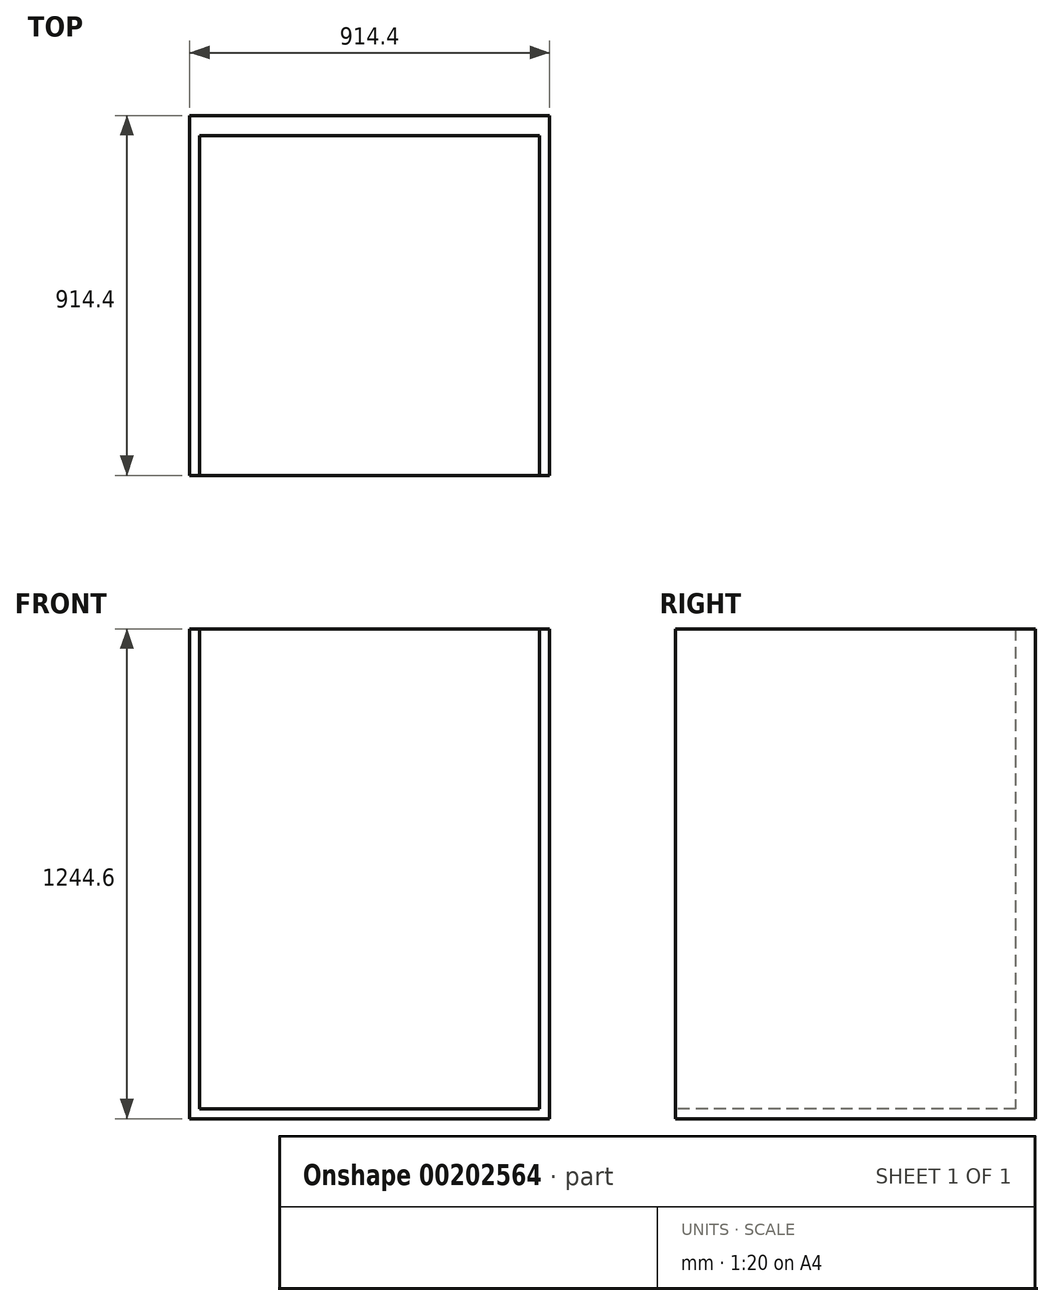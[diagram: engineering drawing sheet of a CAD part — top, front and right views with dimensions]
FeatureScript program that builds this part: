
annotation { "Feature Type Name" : "Feature", "Feature Type Description" : "" }
export const myFeature = defineFeature(function(context is Context, id is Id, definition is map)
    precondition{}
    {
        {
            var Q0;
            Q0=qCreatedBy(makeId("Top.planeOp"),FACE);
            var sketch = newSketch(context, id + "F0", { "sketchPlane" : qUnion([Q0])});
            skLineSegment(sketch, "E0.bottom", {"start": v(0, 0) * mm, "end": v(914.4, 0) * mm});
            skLineSegment(sketch, "E0.top", {"start": v(0, 914.4) * mm, "end": v(914.4, 914.4) * mm});
            skLineSegment(sketch, "E0.left", {"start": v(0, 0) * mm, "end": v(0, 914.4) * mm});
            skLineSegment(sketch, "E0.right", {"start": v(914.4, 0) * mm, "end": v(914.4, 914.4) * mm});
            skSolve(sketch);
        }
        {
            var Q0;
            Q0=makeQuery(id+"F0.imprint","IMPRINT",FACE,{"disambiguationData":[TD([[makeQuery(id+"F0.imprint","IMPRINT",EDGE,{"derivedFrom":sQuery(id+"F0.wireOp",EDGE,"E0.bottom")}),1.0]])]});
            extrude(context, id + "F1", {"entities" : qUnion([Q0]), "depth" : 25.4 * mm});
        }
        {
            var Q0;
            Q0=makeQuery(id+"F1.opExtrude","CAP_FACE",FACE,{"disambiguationData":[OSD([sQuery(id+"F0.wireOp",EDGE,"E0.bottom"),sQuery(id+"F0.wireOp",EDGE,"E0.top"),sQuery(id+"F0.wireOp",EDGE,"E0.left"),sQuery(id+"F0.wireOp",EDGE,"E0.right")])],"isStart":false});
            var sketch = newSketch(context, id + "F2", { "sketchPlane" : qUnion([Q0])});
            skLineSegment(sketch, "E1", {"start": v(0, 0) * mm, "end": v(25.4, 0) * mm});
            skLineSegment(sketch, "E2", {"start": v(25.4, 0) * mm, "end": v(25.4, 863.6) * mm});
            skLineSegment(sketch, "E3", {"start": v(25.4, 863.6) * mm, "end": v(889, 863.6) * mm});
            skLineSegment(sketch, "E4", {"start": v(889, 863.6) * mm, "end": v(889, 0) * mm});
            skSolve(sketch);
        }
        {
            var Q0;
            Q0 = qSketchRegion(id + "F2", true);
            var Q1;
            Q1=makeQuery(id+"F2.imprint","IMPRINT",FACE,{"disambiguationData":[TD([[makeQuery(id+"F2.imprint","IMPRINT",EDGE,{"derivedFrom":sQuery(id+"F2.wireOp",EDGE,"E1")}),1.0]])]});
            extrude(context, id + "F3", {"entities" : qUnion([Q0, Q1]), "operationType" : NewBodyOperationType.ADD, "depth" : 1219.2 * mm});
        }
    });
